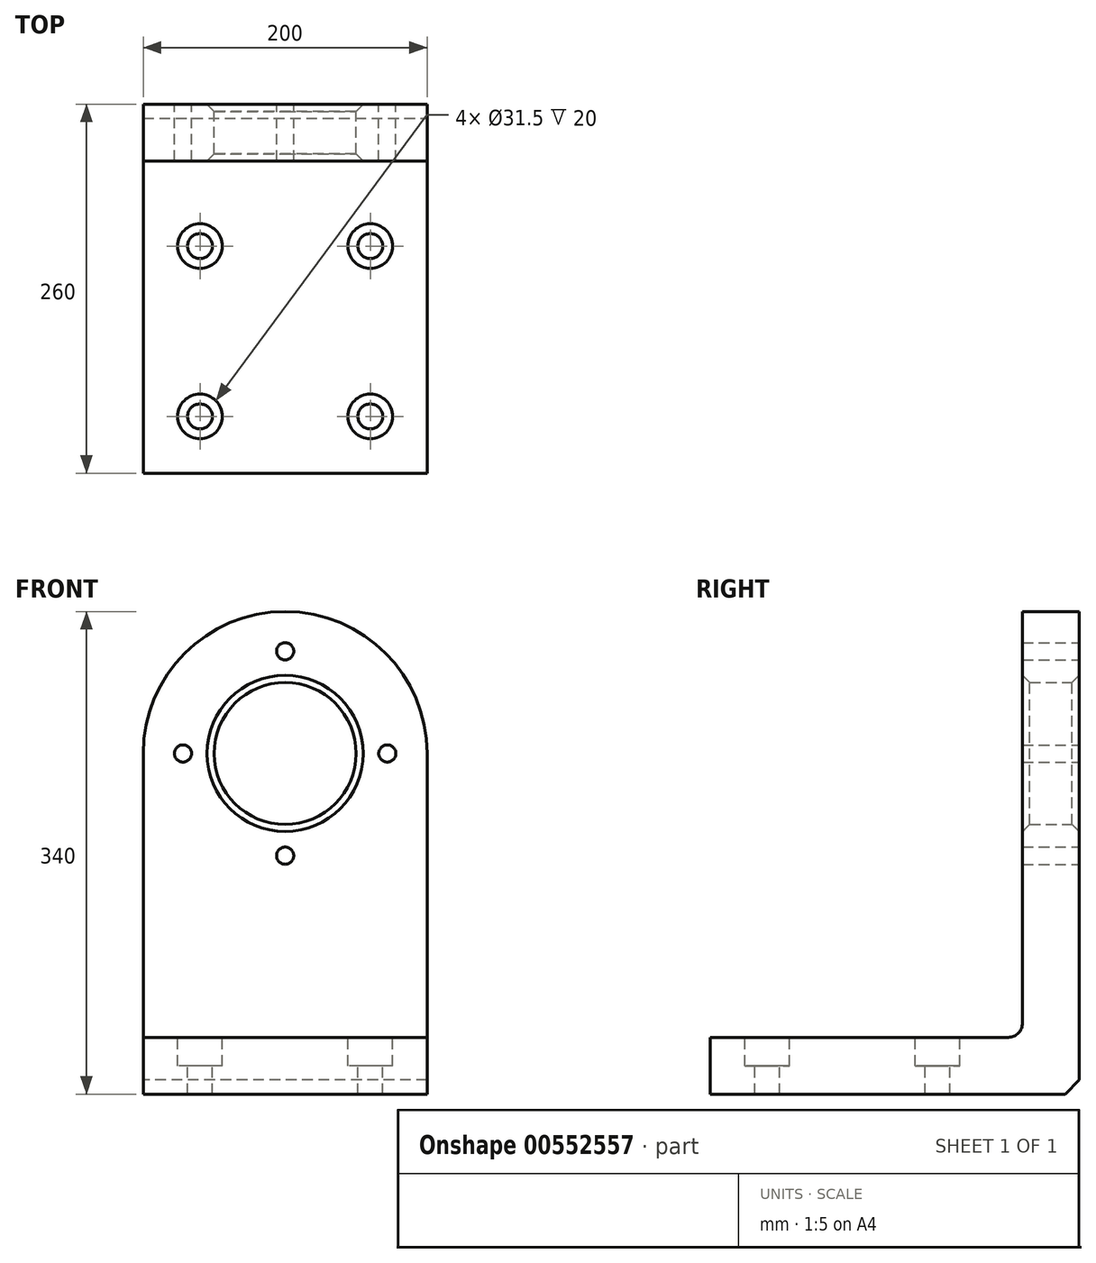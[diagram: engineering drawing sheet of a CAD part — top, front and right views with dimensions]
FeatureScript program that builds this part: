
annotation { "Feature Type Name" : "Feature", "Feature Type Description" : "" }
export const myFeature = defineFeature(function(context is Context, id is Id, definition is map)
    precondition{}
    {
        {
            var Q0;
            Q0=qCreatedBy(makeId("Front.planeOp"),FACE);
            var sketch = newSketch(context, id + "F0", { "sketchPlane" : qUnion([Q0])});
            skLineSegment(sketch, "E0", {"start": v(0, 0) * mm, "end": v(100, 0) * mm});
            skLineSegment(sketch, "E1", {"start": v(100, 0) * mm, "end": v(-100, 0) * mm});
            skLineSegment(sketch, "E2", {"start": v(-100, 0) * mm, "end": v(-100, 200) * mm});
            skLineSegment(sketch, "E3", {"start": v(100, 0) * mm, "end": v(100, 200) * mm});
            skLineSegment(sketch, "E4", {"start": v(-100, 200) * mm, "end": v(100, 200) * mm, "construction": true});
            skArc(sketch, "E5", {"start": v(-100, 200) * mm, "mid": v(0, 300) * mm, "end": v(100, 200) * mm});
            skCircle(sketch, "E6", {"center": v(0, 200) * mm, "radius": 50 * mm});
            skLineSegment(sketch, "E7", {"start": v(0, 300) * mm, "end": v(0, 0) * mm, "construction": true});
            skCircle(sketch, "E8", {"center": v(0, 200) * mm, "radius": 72 * mm, "construction": true});
            skPoint(sketch, "E9", {"position": v(0, 272) * mm});
            skPoint(sketch, "E10", {"position": v(72, 200) * mm});
            skPoint(sketch, "E11", {"position": v(0, 128) * mm});
            skPoint(sketch, "E12", {"position": v(-72, 200) * mm});
            skLineSegment(sketch, "E13", {"start": v(-100, 0) * mm, "end": v(-100, -40) * mm});
            skLineSegment(sketch, "E14", {"start": v(-100, -40) * mm, "end": v(100, -40) * mm});
            skLineSegment(sketch, "E15", {"start": v(100, -40) * mm, "end": v(100, 0) * mm});
            skSolve(sketch);
        }
        {
            var Q0;
            Q0 = qSketchRegion(id + "F0", true);
            extrude(context, id + "F1", {"entities" : qUnion([Q0]), "depth" : 40 * mm, "offsetDistance" : 25 * mm});
        }
        {
            var Q0;
            Q0=makeQuery(id+"F1.opExtrude","SWEPT_FACE",FACE,{"disambiguationData":[OSD([sQuery(id+"F0.wireOp",EDGE,"E6")])]});
            chamfer(context, id + "F2", {"entities" : qUnion([Q0]), "width" : 5 * mm, "tangentPropagation" : true});
        }
        {
            var Q0;
            Q0=sQuery(id+"F0.wireOp",VERTEX,"E9");
            var Q1;
            Q1=sQuery(id+"F0.wireOp",VERTEX,"E10");
            var Q2;
            Q2=sQuery(id+"F0.wireOp",VERTEX,"E11");
            var Q3;
            Q3=sQuery(id+"F0.wireOp",VERTEX,"E12");
            var Q4;
            Q4=makeQuery(id+"F1.opExtrude","SWEPT_BODY",BODY,{"disambiguationData":[OSD([sQuery(id+"F0.wireOp",EDGE,"E1"),sQuery(id+"F0.wireOp",EDGE,"E2"),sQuery(id+"F0.wireOp",EDGE,"E3"),sQuery(id+"F0.wireOp",EDGE,"E5"),sQuery(id+"F0.wireOp",EDGE,"E6")])]});
            hole(context, id + "F3", {"style" : HoleStyle.SIMPLE, "endStyle" : HoleEndStyle.THROUGH, "oppositeDirection" : true, "standardTappedOrClearance" : lookupTablePath({ "standard" : "ISO", "engagement" : "75%", "pitch" : "2 mm", "size" : "M14", "type" : "Tapped" }), "standardBlindInLast" : lookupTablePath({ "standard" : "ISO", "engagement" : "75%", "pitch" : "2 mm", "size" : "M14", "type" : "Tapped" }), "holeDiameter" : 12.1 * mm, "showTappedDepth" : true, "isTappedThrough" : true, "tappedDepth" : 12 * mm, "tapClearance" : 3, "locations" : qUnion([Q0, Q1, Q2, Q3]), "scope" : qUnion([Q4]), "majorDiameter" : 14 * mm});
        }
        {
            var Q0;
            {var subQ0=sQuery(id+"F0.wireOp",EDGE,"E13");Q0=makeQuery(id+"F0.imprint","IMPRINT",FACE,{"disambiguationData":[TD([[makeQuery(id+"F0.imprint","IMPRINT",EDGE,{"derivedFrom":subQ0}),1.0]])]});}
            extrude(context, id + "F4", {"entities" : qUnion([Q0]), "operationType" : NewBodyOperationType.ADD, "depth" : 260 * mm, "offsetDistance" : 25 * mm});
        }
        {
            var Q0;
            Q0=makeQuery(id+"F4.boolean.opBoolean","INTERSECT",EDGE,{"derivedFrom":[makeQuery(id+"F1.opExtrude","CAP_FACE",FACE,{"disambiguationData":[OSD([sQuery(id+"F0.wireOp",EDGE,"E2"),sQuery(id+"F0.wireOp",EDGE,"E3"),sQuery(id+"F0.wireOp",EDGE,"E5"),sQuery(id+"F0.wireOp",EDGE,"E6"),sQuery(id+"F0.wireOp",EDGE,"E13"),sQuery(id+"F0.wireOp",EDGE,"E14"),sQuery(id+"F0.wireOp",EDGE,"E15")])],"isStart":false}),makeQuery(id+"F4.opExtrude","SWEPT_FACE",FACE,{"disambiguationData":[OSD([sQuery(id+"F0.wireOp",EDGE,"E1")])]})]});
            fillet(context, id + "F5", {"entities" : qUnion([Q0]), "radius" : 10 * mm, "tangentPropagation" : true, "allowEdgeOverflow" : false});
        }
        {
            var Q0;
            Q0=makeQuery(id+"F1.opExtrude","CAP_EDGE",EDGE,{"disambiguationData":[OSD([sQuery(id+"F0.wireOp",EDGE,"E14")])],"isStart":true});
            chamfer(context, id + "F6", {"entities" : qUnion([Q0]), "width" : 10 * mm, "tangentPropagation" : true});
        }
        {
            var Q0;
            Q0=qCreatedBy(makeId("Right.planeOp"),FACE);
            var sketch = newSketch(context, id + "F7", { "sketchPlane" : qUnion([Q0])});
            skLineSegment(sketch, "E16.0", {"start": v(-40, 10) * mm, "end": v(-40, 200) * mm});
            skArc(sketch, "E17.0", {"start": v(-40, 10) * mm, "mid": v(-42.93, 2.93) * mm, "end": v(-50, 0) * mm});
            skLineSegment(sketch, "E18.0", {"start": v(-260, 0) * mm, "end": v(-50, 0) * mm});
            skLineSegment(sketch, "E19.0.0", {"start": v(-260, -40) * mm, "end": v(-10, -40) * mm});
            skLineSegment(sketch, "E19.0.1", {"start": v(-10, -40) * mm, "end": v(0, -30) * mm});
            skLineSegment(sketch, "E19.0.2", {"start": v(0, -30) * mm, "end": v(0, 200) * mm});
            skLineSegment(sketch, "E19.0.3", {"start": v(0, 200) * mm, "end": v(-40, 200) * mm});
            skLineSegment(sketch, "E19.0.4", {"start": v(-40, 200) * mm, "end": v(-40, 10) * mm});
            skLineSegment(sketch, "E19.0.6", {"start": v(-50, 0) * mm, "end": v(-260, 0) * mm});
            skLineSegment(sketch, "E19.0.7", {"start": v(-260, 0) * mm, "end": v(-260, -40) * mm});
            skLineSegment(sketch, "E20", {"start": v(-40, 60) * mm, "end": v(-100, 0) * mm});
            skLineSegment(sketch, "E21", {"start": v(-100, 0) * mm, "end": v(-40, 0) * mm});
            skLineSegment(sketch, "E22", {"start": v(-40, 0) * mm, "end": v(-40, 60) * mm});
            skSolve(sketch);
        }
        {
            var Q0;
            {var subQ0=sQuery(id+"F7.wireOp",EDGE,"E17.0");Q0=makeQuery(id+"F7.imprint","IMPRINT",FACE,{"disambiguationData":[TD([[makeQuery(id+"F7.imprint","IMPRINT",EDGE,{"derivedFrom":subQ0}),-1.0]])]});}
            extrude(context, id + "F8", {"entities" : qUnion([Q0]), "operationType" : NewBodyOperationType.ADD, "endBound" : BoundingType.SYMMETRIC, "depth" : 50 * mm, "offsetDistance" : 25 * mm});
        }
        {
            var Q0;
            Q0=qCreatedBy(makeId("Top.planeOp"),FACE);
            var sketch = newSketch(context, id + "F9", { "sketchPlane" : qUnion([Q0])});
            skLineSegment(sketch, "E23", {"start": v(0, 0) * mm, "end": v(0, -260) * mm, "construction": true});
            skLineSegment(sketch, "E24", {"start": v(0, -260) * mm, "end": v(100, -260) * mm, "construction": true});
            skLineSegment(sketch, "E25", {"start": v(0, -260) * mm, "end": v(-100, -260) * mm, "construction": true});
            skLineSegment(sketch, "E26", {"start": v(100, -260) * mm, "end": v(100, -220) * mm, "construction": true});
            skLineSegment(sketch, "E27", {"start": v(100, -220) * mm, "end": v(-100, -220) * mm, "construction": true});
            skLineSegment(sketch, "E28", {"start": v(-100, -220) * mm, "end": v(-100, -260) * mm, "construction": true});
            skPoint(sketch, "E29", {"position": v(-60, -220) * mm});
            skPoint(sketch, "E30", {"position": v(60, -220) * mm});
            skLineSegment(sketch, "E31", {"start": v(-60, -220) * mm, "end": v(-60, -100) * mm, "construction": true});
            skLineSegment(sketch, "E32", {"start": v(-60, -100) * mm, "end": v(60, -100) * mm, "construction": true});
            skLineSegment(sketch, "E33", {"start": v(60, -100) * mm, "end": v(60, -220) * mm, "construction": true});
            skPoint(sketch, "E34", {"position": v(-60, -100) * mm});
            skPoint(sketch, "E35", {"position": v(60, -100) * mm});
            skSolve(sketch);
        }
        {
            var Q0;
            Q0=sQuery(id+"F9.wireOp",VERTEX,"E34");
            var Q1;
            Q1=sQuery(id+"F9.wireOp",VERTEX,"E35");
            var Q2;
            Q2=sQuery(id+"F9.wireOp",VERTEX,"E30");
            var Q3;
            Q3=sQuery(id+"F9.wireOp",VERTEX,"E29");
            var Q4;
            Q4=makeQuery(id+"F1.opExtrude","SWEPT_BODY",BODY,{"disambiguationData":[OSD([sQuery(id+"F0.wireOp",EDGE,"E2"),sQuery(id+"F0.wireOp",EDGE,"E3"),sQuery(id+"F0.wireOp",EDGE,"E5"),sQuery(id+"F0.wireOp",EDGE,"E6"),sQuery(id+"F0.wireOp",EDGE,"E13"),sQuery(id+"F0.wireOp",EDGE,"E14"),sQuery(id+"F0.wireOp",EDGE,"E15")])]});
            hole(context, id + "F10", {"style" : HoleStyle.C_BORE, "endStyle" : HoleEndStyle.THROUGH, "holeDiameter" : 17.5 * mm, "cBoreDiameter" : 31.5 * mm, "cBoreDepth" : 20 * mm, "isTappedThrough" : true, "tappedDepth" : 12 * mm, "tapClearance" : 3, "locations" : qUnion([Q0, Q1, Q2, Q3]), "scope" : qUnion([Q4])});
        }
    });
